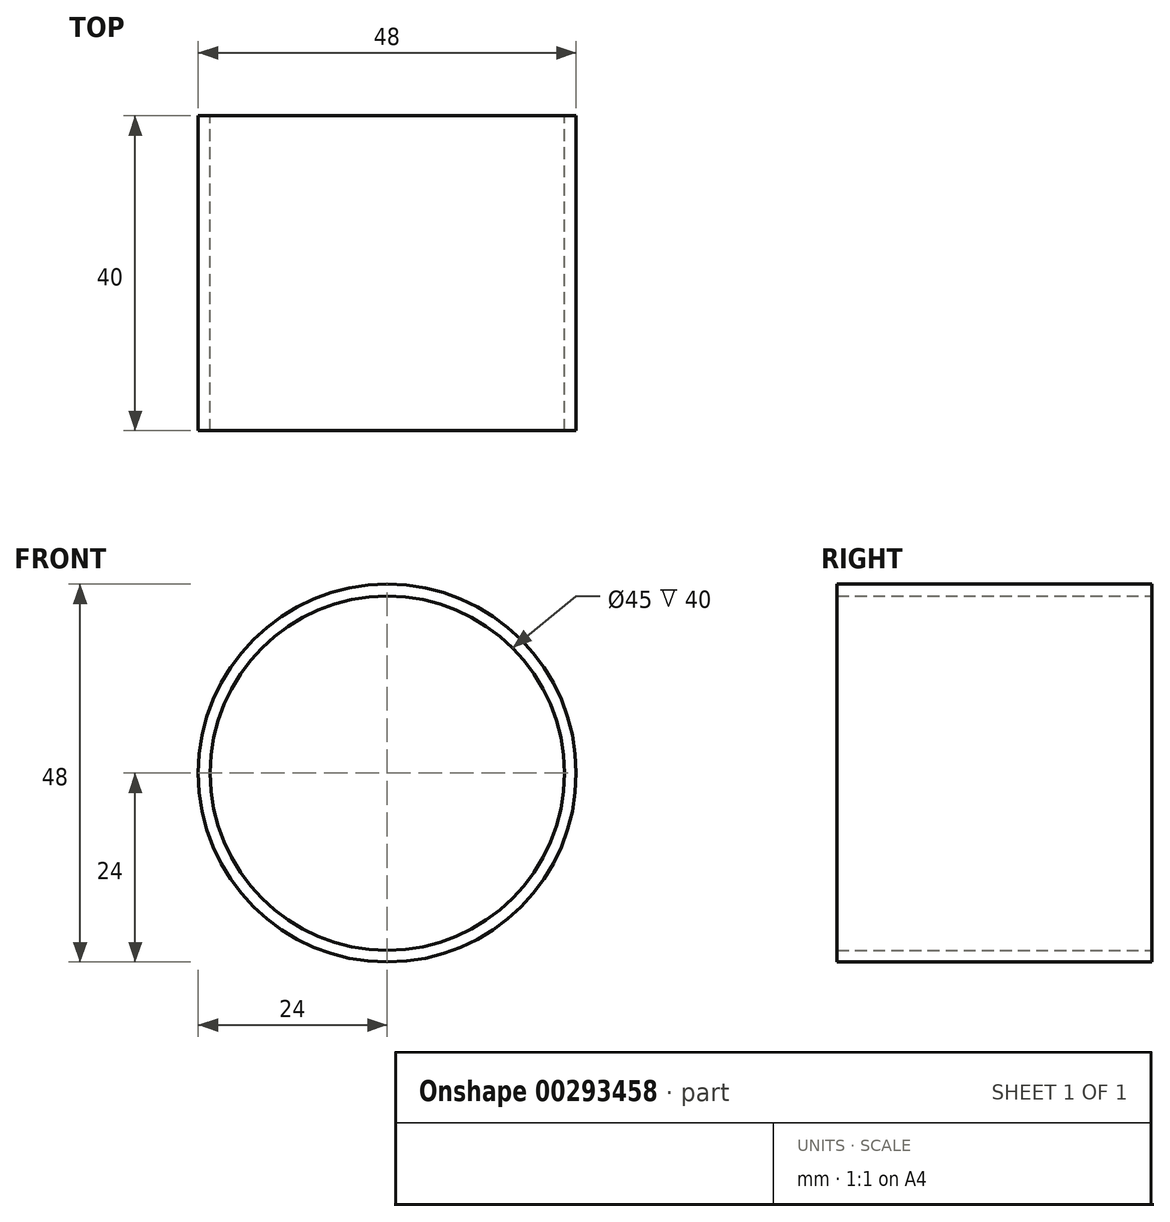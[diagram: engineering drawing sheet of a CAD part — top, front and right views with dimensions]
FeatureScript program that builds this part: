
annotation { "Feature Type Name" : "Feature", "Feature Type Description" : "" }
export const myFeature = defineFeature(function(context is Context, id is Id, definition is map)
    precondition{}
    {
        {
            var Q0;
            Q0=qCreatedBy(makeId("Front.planeOp"),FACE);
            var sketch = newSketch(context, id + "F0", { "sketchPlane" : qUnion([Q0])});
            skCircle(sketch, "E0", {"center": v(0, 0) * mm, "radius": 24 * mm});
            skCircle(sketch, "E1", {"center": v(0, 0) * mm, "radius": 22.5 * mm});
            skSolve(sketch);
        }
        {
            var Q0;
            Q0=makeQuery(id+"F0.imprint","IMPRINT",FACE,{"disambiguationData":[TD([[makeQuery(id+"F0.imprint","IMPRINT",EDGE,{"derivedFrom":sQuery(id+"F0.wireOp",EDGE,"E0")}),1.0]])]});
            extrude(context, id + "F1", {"entities" : qUnion([Q0]), "depth" : 40 * mm, "offsetDistance" : 25 * mm});
        }
    });
